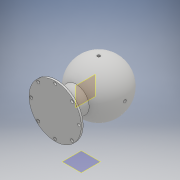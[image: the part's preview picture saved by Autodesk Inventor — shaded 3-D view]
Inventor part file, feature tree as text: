
AUTODESK INVENTOR PART (.ipt)
format: ipt  version: 2017 (Build 210142000, 142)  size: 214,016 bytes
history: native  units: mm
features: sketch x4, extrude x3, plane x2, revolve x1
ambient origin geometry x8: Origin, YZ Plane, XZ Plane, XY Plane, X Axis, Y Axis, Z Axis, Center Point
bodies: Solid1 (feature_tree)
feature tree (10):
  revolve  "Revolution1"  [1 undecoded]
  extrude  "Extrusion1"  Depth=20.0mm
  plane  "Work Plane1"
  extrude  "Extrusion3"  TaperAngle=90.0deg  [1 undecoded]
  plane  "Work Plane2"
  extrude  "Extrusion5"  TaperAngle=45.0deg  [1 undecoded]
  sketch  "Sketch1"  dims[d0=60.0mm d3=20.0mm]
  sketch  "Sketch2"  dims[d4=30.0mm d5=20.0mm]
  sketch  "Sketch4"  dims[d6=1.0mm d7=90.0deg]
  sketch  "Sketch6"  dims[d8=3.2mm d9=45.0deg d10=3.52mm d11=3.2mm d12=10.0mm d13=0.0mm d16=60.0mm d17=3.2mm d18=73.75mm d19=0.0mm d22=60.0mm d23=3.2mm d24=74.75mm d25=0.0mm]
note: 3 required parameter values undecoded (feature->parameter linkage not recoverable at this tier; creation-order binding heuristic only, values carry confidence <= 0.55)